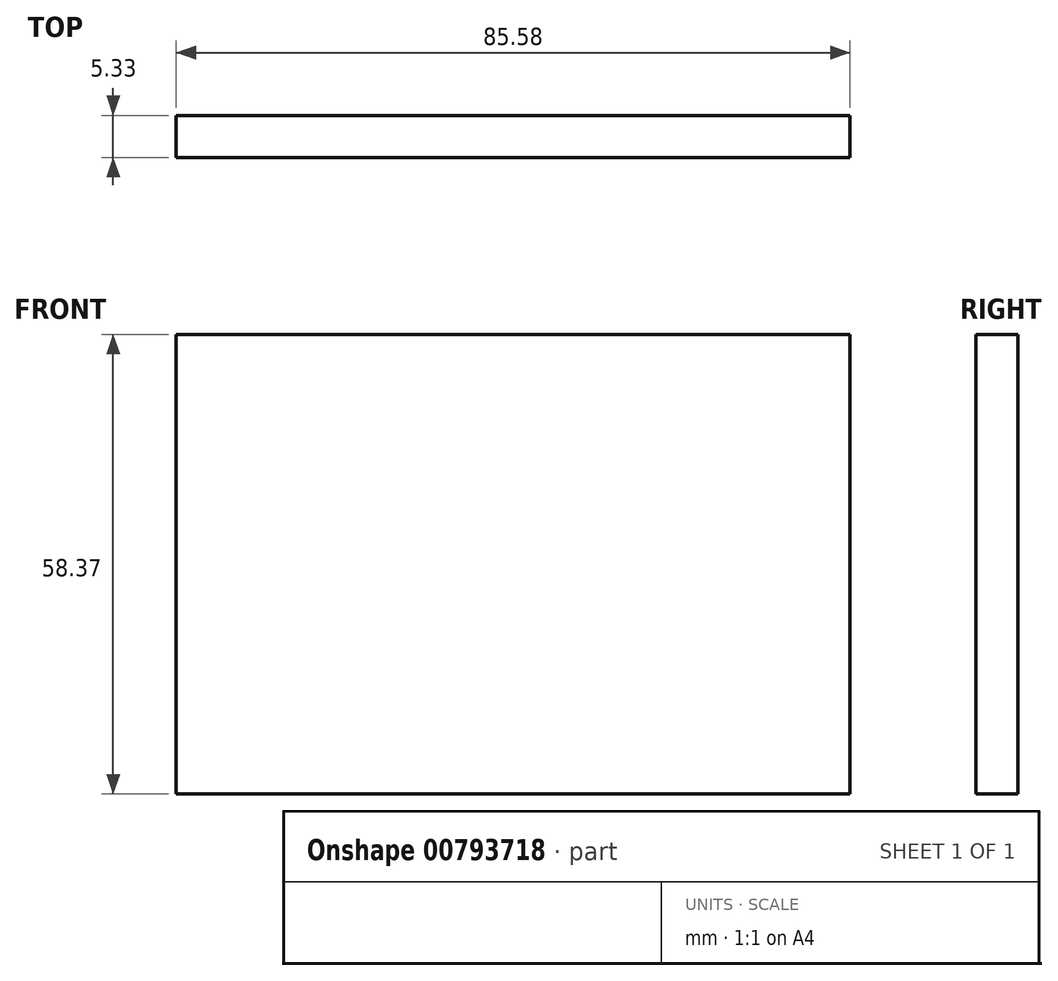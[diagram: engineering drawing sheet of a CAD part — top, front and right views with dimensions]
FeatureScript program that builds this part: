
annotation { "Feature Type Name" : "Feature", "Feature Type Description" : "" }
export const myFeature = defineFeature(function(context is Context, id is Id, definition is map)
    precondition{}
    {
        {
            var Q0;
            Q0=qCreatedBy(makeId("Front.planeOp"),FACE);
            var sketch = newSketch(context, id + "F0", { "sketchPlane" : qUnion([Q0])});
            skLineSegment(sketch, "E0.bottom", {"start": v(-32.46, 27.7) * mm, "end": v(53.12, 27.7) * mm});
            skLineSegment(sketch, "E0.top", {"start": v(-32.46, -30.66) * mm, "end": v(53.12, -30.66) * mm});
            skLineSegment(sketch, "E0.left", {"start": v(-32.46, 27.7) * mm, "end": v(-32.46, -30.66) * mm});
            skLineSegment(sketch, "E0.right", {"start": v(53.12, 27.7) * mm, "end": v(53.12, -30.66) * mm});
            skSolve(sketch);
        }
        {
            var Q0;
            Q0 = qSketchRegion(id + "F0", true);
            extrude(context, id + "F1", {"entities" : qUnion([Q0]), "depth" : 5.33 * mm, "offsetDistance" : 25.4 * mm});
        }
    });
